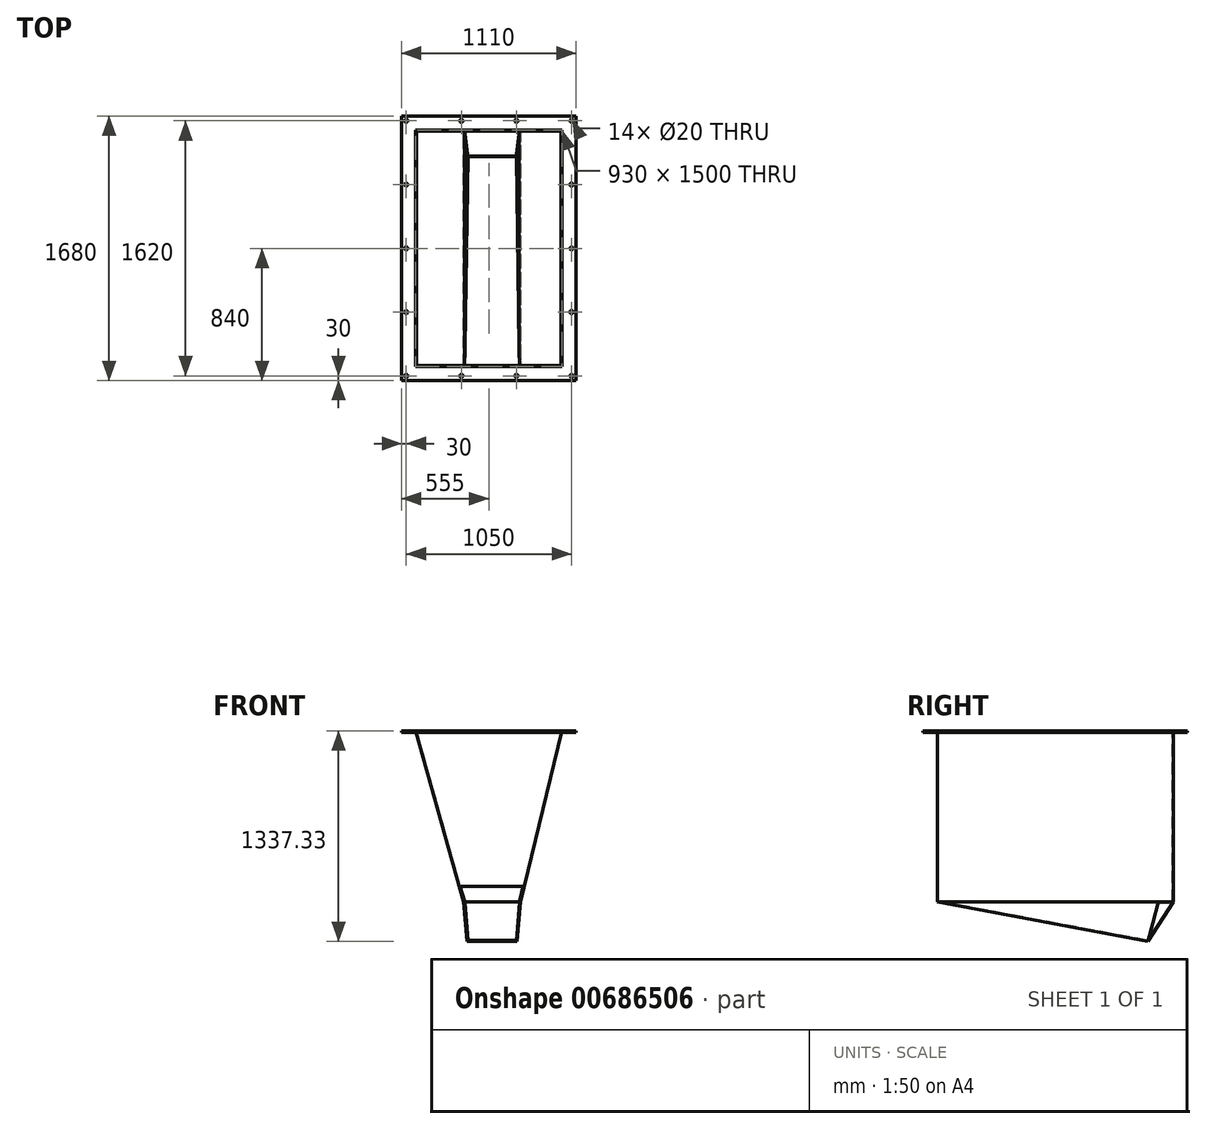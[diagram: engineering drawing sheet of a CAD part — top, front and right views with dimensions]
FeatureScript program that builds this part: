
annotation { "Feature Type Name" : "Feature", "Feature Type Description" : "" }
export const myFeature = defineFeature(function(context is Context, id is Id, definition is map)
    precondition{}
    {
        {
            var Q0;
            Q0=qCreatedBy(makeId("Front.planeOp"),FACE);
            var sketch = newSketch(context, id + "F0", { "sketchPlane" : qUnion([Q0])});
            skLineSegment(sketch, "E0", {"start": v(-465, 550.08) * mm, "end": v(465, 550.08) * mm});
            skLineSegment(sketch, "E1", {"start": v(465, 550.08) * mm, "end": v(200, -536.9) * mm});
            skLineSegment(sketch, "E2", {"start": v(200, -536.9) * mm, "end": v(-160, -536.9) * mm});
            skLineSegment(sketch, "E3", {"start": v(-160, -536.9) * mm, "end": v(-465, 550.08) * mm});
            skSolve(sketch);
        }
        {
            var Q0;
            Q0 = qSketchRegion(id + "F0", true);
            extrude(context, id + "F1", {"entities" : qUnion([Q0]), "oppositeDirection" : true, "depth" : 1500 * mm, "offsetDistance" : 25 * mm});
        }
        {
            var Q0;
            Q0=makeQuery(id+"F1.opExtrude","CAP_EDGE",EDGE,{"disambiguationData":[OSD([sQuery(id+"F0.wireOp",EDGE,"E2")])],"isStart":true});
            cPlane(context, id + "F2", {"entities" : qUnion([Q0]), "cplaneType" : CPlaneType.LINE_ANGLE, "offset" : 25 * mm, "angle" : 79.4 * degree, "oppositeDirection" : true, "width" : 150 * mm, "height" : 150 * mm});
        }
        {
            var Q0;
            Q0=qCreatedBy(id+"F2.planeOp",FACE);
            var sketch = newSketch(context, id + "F3", { "sketchPlane" : qUnion([Q0])});
            skLineSegment(sketch, "E4", {"start": v(-160, -98.76) * mm, "end": v(200, -98.76) * mm});
            skLineSegment(sketch, "E5", {"start": v(200, -98.76) * mm, "end": v(180, -1459.28) * mm});
            skLineSegment(sketch, "E6", {"start": v(180, -1459.28) * mm, "end": v(-140, -1459.28) * mm});
            skLineSegment(sketch, "E7", {"start": v(-140, -1459.28) * mm, "end": v(-160, -98.76) * mm});
            skLineSegment(sketch, "E8", {"start": v(20, -329.35) * mm, "end": v(20, -1759.71) * mm, "construction": true});
            skPoint(sketch, "E8.startSnap0", {"position": v(20, -98.76) * mm});
            skSolve(sketch);
        }
        {
            var Q0;
            Q0=makeQuery(id+"F3.imprint","IMPRINT",FACE,{"disambiguationData":[TD([[makeQuery(id+"F3.imprint","IMPRINT",EDGE,{"derivedFrom":sQuery(id+"F3.wireOp",EDGE,"E4")}),-1.0]])]});
            var Q1;
            Q1=makeQuery(id+"F1.opExtrude","SWEPT_FACE",FACE,{"disambiguationData":[OSD([sQuery(id+"F0.wireOp",EDGE,"E2")])]});
            extrude(context, id + "F4", {"entities" : qUnion([Q0]), "operationType" : NewBodyOperationType.ADD, "endBound" : BoundingType.UP_TO_SURFACE, "oppositeDirection" : true, "depth" : 25 * mm, "endBoundEntityFace" : qUnion([Q1]), "offsetDistance" : 25 * mm, "hasDraft" : true, "draftAngle" : 4.5 * degree});
        }
        {
            var Q0;
            Q0=makeQuery(id+"F1.opExtrude","CAP_EDGE",EDGE,{"disambiguationData":[OSD([sQuery(id+"F0.wireOp",EDGE,"E2")])],"isStart":false});
            cPlane(context, id + "F5", {"entities" : qUnion([Q0]), "cplaneType" : CPlaneType.LINE_ANGLE, "offset" : 25 * mm, "angle" : 33 * degree, "width" : 150 * mm, "height" : 150 * mm});
        }
        {
            var Q0;
            Q0=qCreatedBy(id+"F5.planeOp",FACE);
            var sketch = newSketch(context, id + "F6", { "sketchPlane" : qUnion([Q0])});
            skLineSegment(sketch, "E9", {"start": v(200, 366.68) * mm, "end": v(-160, 366.68) * mm});
            skLineSegment(sketch, "E10", {"start": v(-160, 366.68) * mm, "end": v(-140, 68.17) * mm});
            skLineSegment(sketch, "E11", {"start": v(-140, 68.17) * mm, "end": v(180, 68.17) * mm});
            skLineSegment(sketch, "E12", {"start": v(180, 68.17) * mm, "end": v(200, 366.68) * mm});
            skSolve(sketch);
        }
        {
            var Q0;
            Q0=makeQuery(id+"F6.imprint","IMPRINT",FACE,{"disambiguationData":[TD([[makeQuery(id+"F6.imprint","IMPRINT",EDGE,{"derivedFrom":sQuery(id+"F6.wireOp",EDGE,"E9")}),1.0]])]});
            var Q1;
            Q1=makeQuery(id+"F4.opExtrude","SWEPT_FACE",FACE,{"disambiguationData":[OSD([sQuery(id+"F3.wireOp",EDGE,"E6")])]});
            var Q2;
            Q2=makeQuery(id+"F1.opExtrude","SWEPT_BODY",BODY,{"disambiguationData":[OSD([sQuery(id+"F0.wireOp",EDGE,"E0"),sQuery(id+"F0.wireOp",EDGE,"E1"),sQuery(id+"F0.wireOp",EDGE,"E2"),sQuery(id+"F0.wireOp",EDGE,"E3")])]});
            extrude(context, id + "F7", {"entities" : qUnion([Q0]), "operationType" : NewBodyOperationType.ADD, "endBound" : BoundingType.UP_TO_BODY, "depth" : 25 * mm, "endBoundEntityFace" : qUnion([Q1]), "endBoundEntityBody" : qUnion([Q2]), "offsetDistance" : 25 * mm, "hasDraft" : true, "draftAngle" : 2.5 * degree});
        }
        {
            var Q0;
            Q0=makeQuery(id+"F1.opExtrude","SWEPT_FACE",FACE,{"disambiguationData":[OSD([sQuery(id+"F0.wireOp",EDGE,"E0")])]});
            shell(context, id + "F8", {"entities" : qUnion([Q0]), "thickness" : 6 * mm});
        }
        {
            var Q0;
            Q0=makeQuery(id+"F4.opExtrude","CAP_FACE",FACE,{"disambiguationData":[OSD([sQuery(id+"F3.wireOp",EDGE,"E4"),sQuery(id+"F3.wireOp",EDGE,"E5"),sQuery(id+"F3.wireOp",EDGE,"E6"),sQuery(id+"F3.wireOp",EDGE,"E7")])],"isStart":true});
            var sketch = newSketch(context, id + "F9", { "sketchPlane" : qUnion([Q0])});
            skLineSegment(sketch, "E13", {"start": v(-134, -1453.41) * mm, "end": v(-153.83, -104.76) * mm});
            skLineSegment(sketch, "E14", {"start": v(-153.83, -104.76) * mm, "end": v(194, -104.76) * mm});
            skLineSegment(sketch, "E15", {"start": v(194, -104.76) * mm, "end": v(174.17, -1453.41) * mm});
            skLineSegment(sketch, "E16", {"start": v(174.17, -1453.41) * mm, "end": v(-134, -1453.41) * mm});
            skSolve(sketch);
        }
        {
            var Q0;
            Q0 = qSketchRegion(id + "F9", true);
            extrude(context, id + "F10", {"entities" : qUnion([Q0]), "operationType" : NewBodyOperationType.REMOVE, "oppositeDirection" : true, "depth" : 6 * mm, "offsetDistance" : 25 * mm});
        }
        {
            var Q0;
            Q0=makeQuery(id+"F1.opExtrude","SWEPT_FACE",FACE,{"disambiguationData":[OSD([sQuery(id+"F0.wireOp",EDGE,"E0")])]});
            var sketch = newSketch(context, id + "F11", { "sketchPlane" : qUnion([Q0])});
            skLineSegment(sketch, "E17", {"start": v(-465, 0) * mm, "end": v(-465, 1500) * mm});
            skLineSegment(sketch, "E18", {"start": v(-465, 1500) * mm, "end": v(465, 1500) * mm});
            skLineSegment(sketch, "E19", {"start": v(465, 1500) * mm, "end": v(465, 0) * mm});
            skLineSegment(sketch, "E20", {"start": v(465, 0) * mm, "end": v(-465, 0) * mm});
            skLineSegment(sketch, "E21.bottom", {"start": v(-555, -90) * mm, "end": v(555, -90) * mm});
            skLineSegment(sketch, "E21.top", {"start": v(-555, 1590) * mm, "end": v(555, 1590) * mm});
            skLineSegment(sketch, "E21.left", {"start": v(-555, -90) * mm, "end": v(-555, 1590) * mm});
            skLineSegment(sketch, "E21.right", {"start": v(555, -90) * mm, "end": v(555, 1590) * mm});
            skSolve(sketch);
        }
        {
            var Q0;
            Q0 = qSketchRegion(id + "F11", true);
            extrude(context, id + "F12", {"entities" : qUnion([Q0]), "oppositeDirection" : true, "depth" : 10 * mm, "offsetDistance" : 25 * mm});
        }
        {
            var Q0;
            Q0=makeQuery(id+"F12.opExtrude","CAP_FACE",FACE,{"disambiguationData":[OSD([sQuery(id+"F11.wireOp",EDGE,"E17"),sQuery(id+"F11.wireOp",EDGE,"E18"),sQuery(id+"F11.wireOp",EDGE,"E19"),sQuery(id+"F11.wireOp",EDGE,"E20"),sQuery(id+"F11.wireOp",EDGE,"E21.bottom"),sQuery(id+"F11.wireOp",EDGE,"E21.top"),sQuery(id+"F11.wireOp",EDGE,"E21.left"),sQuery(id+"F11.wireOp",EDGE,"E21.right")])],"isStart":true});
            var sketch = newSketch(context, id + "F13", { "sketchPlane" : qUnion([Q0])});
            skCircle(sketch, "E22", {"center": v(-525, 1560) * mm, "radius": 10 * mm});
            skCircle(sketch, "E23", {"center": v(-175, 1560) * mm, "radius": 10 * mm});
            skCircle(sketch, "E24", {"center": v(175, 1560) * mm, "radius": 10 * mm});
            skCircle(sketch, "E25", {"center": v(525, 1560) * mm, "radius": 10 * mm});
            skLineSegment(sketch, "E26", {"start": v(-770.34, 750) * mm, "end": v(1029.88, 750) * mm, "construction": true});
            skPoint(sketch, "E26.startSnap0", {"position": v(-555, 750) * mm});
            skLineSegment(sketch, "E27", {"start": v(0, 1815.12) * mm, "end": v(0, -396.85) * mm, "construction": true});
            skPoint(sketch, "E27.startSnap0", {"position": v(0, 1590) * mm});
            skCircle(sketch, "E28", {"center": v(525, 1155) * mm, "radius": 10 * mm});
            skCircle(sketch, "E29", {"center": v(525, 750) * mm, "radius": 10 * mm});
            skCircle(sketch, "E30", {"center": v(525, 345) * mm, "radius": 10 * mm});
            skCircle(sketch, "E31", {"center": v(525, -60) * mm, "radius": 10 * mm});
            skCircle(sketch, "E32.MirrorC", {"center": v(-525, 1155) * mm, "radius": 10 * mm});
            skCircle(sketch, "E33.MirrorC", {"center": v(-525, 750) * mm, "radius": 10 * mm});
            skCircle(sketch, "E34.MirrorC", {"center": v(-525, 345) * mm, "radius": 10 * mm});
            skCircle(sketch, "E35.MirrorC", {"center": v(-525, -60) * mm, "radius": 10 * mm});
            skCircle(sketch, "E36.MirrorC", {"center": v(175, -60) * mm, "radius": 10 * mm});
            skCircle(sketch, "E37.MirrorC", {"center": v(-175, -60) * mm, "radius": 10 * mm});
            skSolve(sketch);
        }
        {
            var Q0;
            Q0 = qSketchRegion(id + "F13", true);
            extrude(context, id + "F14", {"entities" : qUnion([Q0]), "operationType" : NewBodyOperationType.REMOVE, "oppositeDirection" : true, "depth" : 10 * mm, "offsetDistance" : 25 * mm});
        }
        {
            var Q0;
            Q0=qCreatedBy(makeId("Front.planeOp"),FACE);
            var sketch = newSketch(context, id + "F15", { "sketchPlane" : qUnion([Q0])});
            skLineSegment(sketch, "E38", {"start": v(-150.96, -546.9) * mm, "end": v(-181.83, -436.9) * mm});
            skLineSegment(sketch, "E39", {"start": v(-181.83, -436.9) * mm, "end": v(218.2, -436.9) * mm});
            skLineSegment(sketch, "E40", {"start": v(218.2, -436.9) * mm, "end": v(191.39, -546.9) * mm});
            skLineSegment(sketch, "E41", {"start": v(191.39, -546.9) * mm, "end": v(-150.96, -546.9) * mm});
            skSolve(sketch);
        }
        {
            var Q0;
            Q0 = qSketchRegion(id + "F15", true);
            extrude(context, id + "F16", {"entities" : qUnion([Q0]), "operationType" : NewBodyOperationType.REMOVE, "oppositeDirection" : true, "depth" : 8 * mm, "offsetDistance" : 25 * mm});
        }
    });
